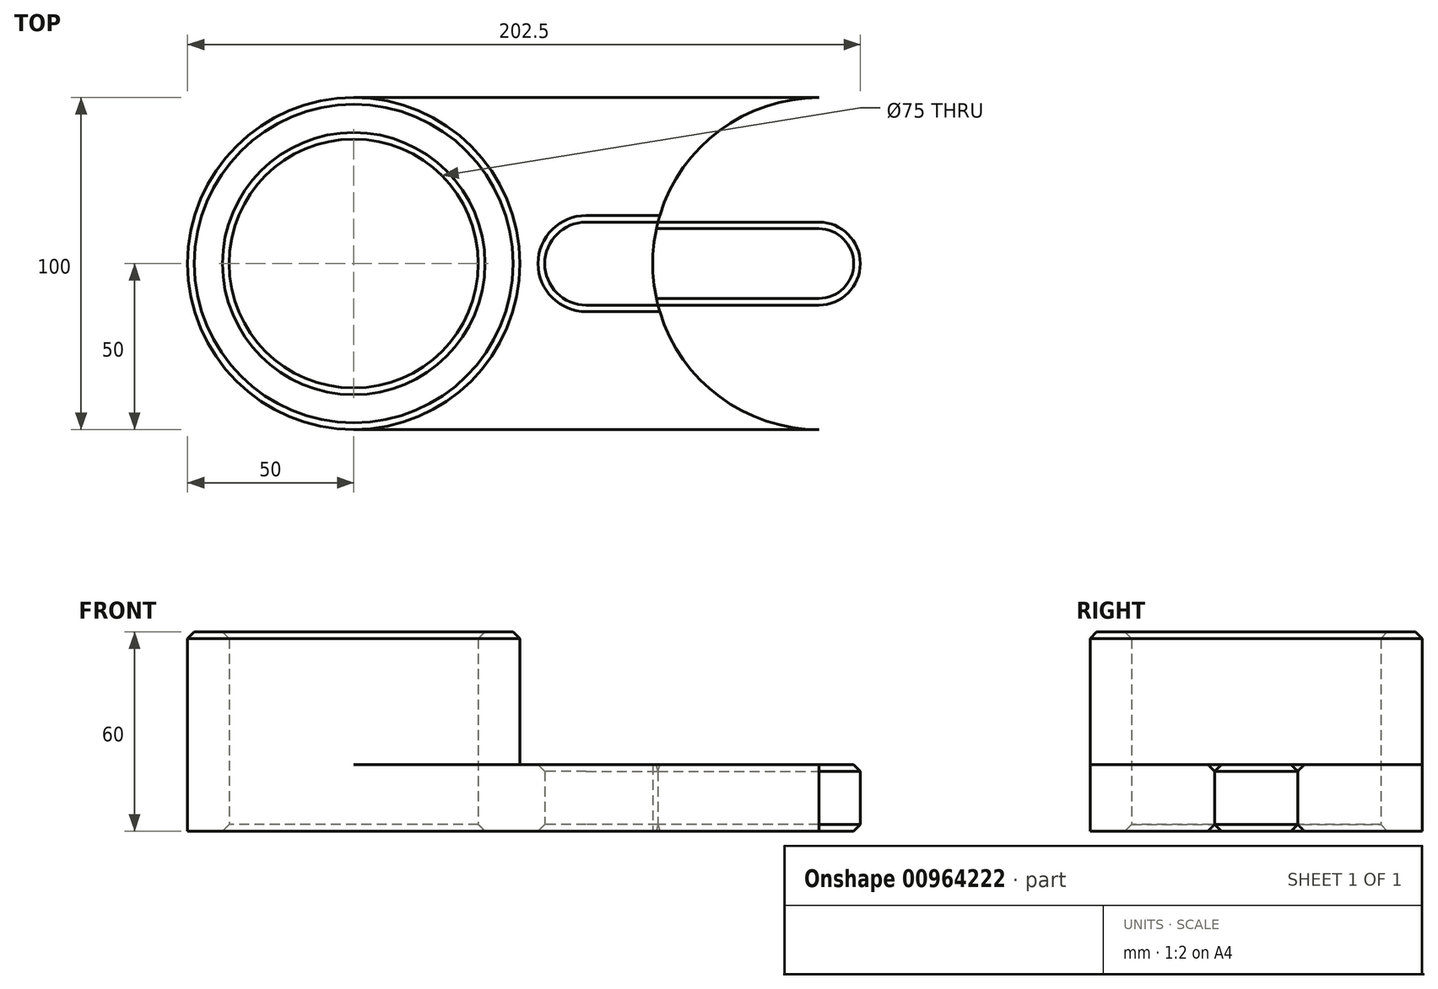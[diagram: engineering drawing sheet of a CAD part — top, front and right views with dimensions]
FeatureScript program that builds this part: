
annotation { "Feature Type Name" : "Feature", "Feature Type Description" : "" }
export const myFeature = defineFeature(function(context is Context, id is Id, definition is map)
    precondition{}
    {
        {
            var Q0;
            Q0=qCreatedBy(makeId("Top.planeOp"),FACE);
            var sketch = newSketch(context, id + "F0", { "sketchPlane" : qUnion([Q0])});
            skCircle(sketch, "E0", {"center": v(-70, 0) * mm, "radius": 50 * mm});
            skCircle(sketch, "E1", {"center": v(70, 0) * mm, "radius": 50 * mm});
            skCircle(sketch, "E2", {"center": v(-70, 0) * mm, "radius": 37.5 * mm});
            skLineSegment(sketch, "E3", {"start": v(-70, 50) * mm, "end": v(70, 50) * mm});
            skLineSegment(sketch, "E4", {"start": v(-70, -50) * mm, "end": v(70, -50) * mm});
            skLineSegment(sketch, "E5", {"start": v(70, 0) * mm, "end": v(0, 0) * mm, "construction": true});
            skArc(sketch, "E6.0.startCap", {"start": v(70, 12.5) * mm, "mid": v(82.5, 0) * mm, "end": v(70, -12.5) * mm});
            skArc(sketch, "E6.0.endCap", {"start": v(0, -12.5) * mm, "mid": v(-12.5, 0) * mm, "end": v(0, 12.5) * mm});
            skLineSegment(sketch, "E6.0.left", {"start": v(70, -12.5) * mm, "end": v(0, -12.5) * mm});
            skLineSegment(sketch, "E6.0.right", {"start": v(70, 12.5) * mm, "end": v(0, 12.5) * mm});
            skLineSegment(sketch, "E7", {"start": v(70, 0) * mm, "end": v(-181.54, 0) * mm, "construction": true});
            skSolve(sketch);
        }
        {
            var Q0;
            {var subQ3=sQuery(id+"F0.wireOp",EDGE,"E6.0.startCap");Q0=makeQuery(id+"F0.imprint","IMPRINT",FACE,{"disambiguationData":[TD([[makeQuery(id+"F0.imprint","IMPRINT",EDGE,{"derivedFrom":subQ3}),1.0]])]});}
            var Q1;
            {var subQ4=sQuery(id+"F0.wireOp",EDGE,"E3");Q1=makeQuery(id+"F0.imprint","IMPRINT",FACE,{"disambiguationData":[TD([[makeQuery(id+"F0.imprint","IMPRINT",EDGE,{"derivedFrom":subQ4}),-1.0]])]});}
            var Q2;
            Q2=makeQuery(id+"F0.imprint","IMPRINT",FACE,{"disambiguationData":[TD([[makeQuery(id+"F0.imprint","IMPRINT",EDGE,{"derivedFrom":sQuery(id+"F0.wireOp",EDGE,"E2")}),-1.0]])]});
            extrude(context, id + "F1", {"entities" : qUnion([Q0, Q1, Q2]), "depth" : 20 * mm, "offsetDistance" : 25 * mm});
        }
        {
            var Q0;
            Q0 = qSketchRegion(id + "FsgrIsFDFfhdDx1_0", true);
            var Q1;
            Q1=makeQuery(id+"F0.imprint","IMPRINT",FACE,{"disambiguationData":[TD([[makeQuery(id+"F0.imprint","IMPRINT",EDGE,{"derivedFrom":sQuery(id+"F0.wireOp",EDGE,"E2")}),-1.0]])]});
            extrude(context, id + "F2", {"entities" : qUnion([Q0, Q1]), "operationType" : NewBodyOperationType.ADD, "depth" : 60 * mm, "offsetDistance" : 25 * mm});
        }
        {
            var Q0;
            Q0=makeQuery(id+"F2.opExtrude","CAP_EDGE",EDGE,{"disambiguationData":[OSD([sQuery(id+"F0.wireOp",EDGE,"E2")])],"isStart":false});
            var Q1;
            Q1=makeQuery(id+"F2.opExtrude","CAP_EDGE",EDGE,{"disambiguationData":[OSD([sQuery(id+"F0.wireOp",EDGE,"E0")])],"isStart":false});
            chamfer(context, id + "F3", {"entities" : qUnion([Q0, Q1]), "width" : 2 * mm, "tangentPropagation" : true});
        }
        {
            var Q0;
            Q0=makeQuery(id+"F1.opExtrude","CAP_EDGE",EDGE,{"disambiguationData":[OSD([sQuery(id+"F0.wireOp",EDGE,"E6.0.right")])],"isStart":false});
            chamfer(context, id + "F4", {"entities" : qUnion([Q0]), "width" : 2 * mm, "tangentPropagation" : true});
        }
        {
            var Q0;
            Q0=makeQuery(id+"F1.opExtrude","CAP_EDGE",EDGE,{"disambiguationData":[OSD([sQuery(id+"F0.wireOp",EDGE,"E6.0.left")])],"isStart":true});
            var Q1;
            Q1=makeQuery(id+"F1.opExtrude","CAP_EDGE",EDGE,{"disambiguationData":[OSD([sQuery(id+"F0.wireOp",EDGE,"E2")])],"isStart":true});
            chamfer(context, id + "F5", {"entities" : qUnion([Q0, Q1]), "width" : 2 * mm, "tangentPropagation" : true});
        }
    });
